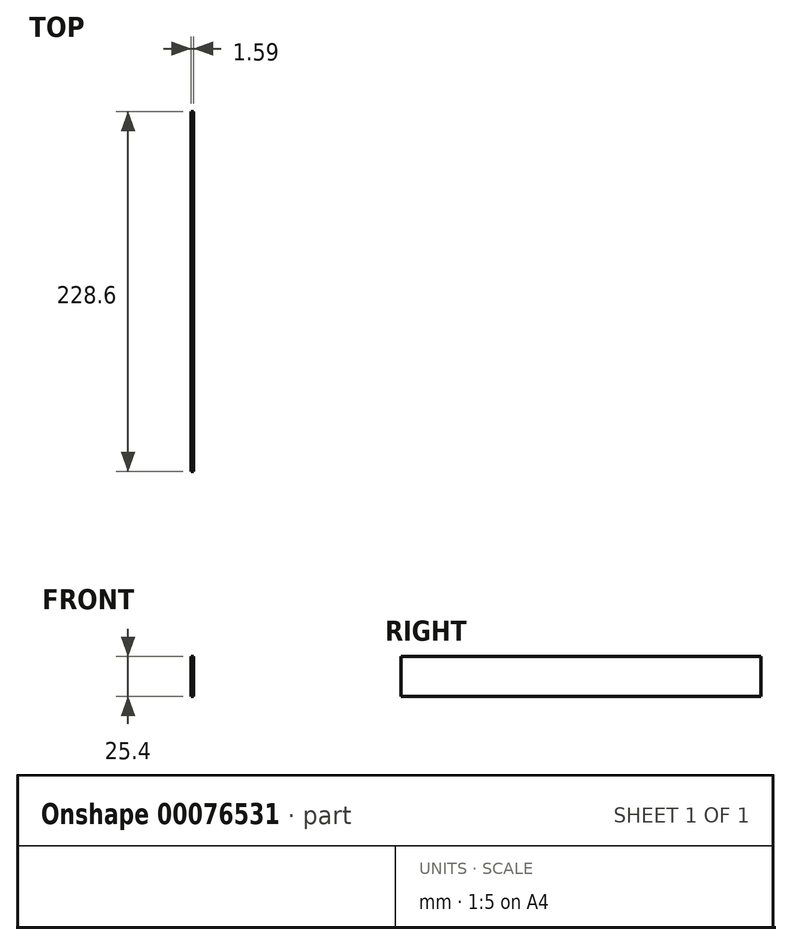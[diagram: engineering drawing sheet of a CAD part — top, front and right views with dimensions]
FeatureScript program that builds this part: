
annotation { "Feature Type Name" : "Feature", "Feature Type Description" : "" }
export const myFeature = defineFeature(function(context is Context, id is Id, definition is map)
    precondition{}
    {
        {
            var Q0;
            Q0=qCreatedBy(makeId("Front.planeOp"),FACE);
            var sketch = newSketch(context, id + "F0", { "sketchPlane" : qUnion([Q0])});
            skLineSegment(sketch, "E0.bottom", {"start": v(0, 0) * mm, "end": v(1.59, 0) * mm});
            skLineSegment(sketch, "E0.top", {"start": v(0, 25.4) * mm, "end": v(1.59, 25.4) * mm});
            skLineSegment(sketch, "E0.left", {"start": v(0, 0) * mm, "end": v(0, 25.4) * mm});
            skLineSegment(sketch, "E0.right", {"start": v(1.59, 0) * mm, "end": v(1.59, 25.4) * mm});
            skSolve(sketch);
        }
        {
            var Q0;
            Q0=qSketchRegion(id+"F0",true);
            extrude(context, id + "F1", {"entities" : qUnion([Q0]), "depth" : 228.6 * mm});
        }
    });
